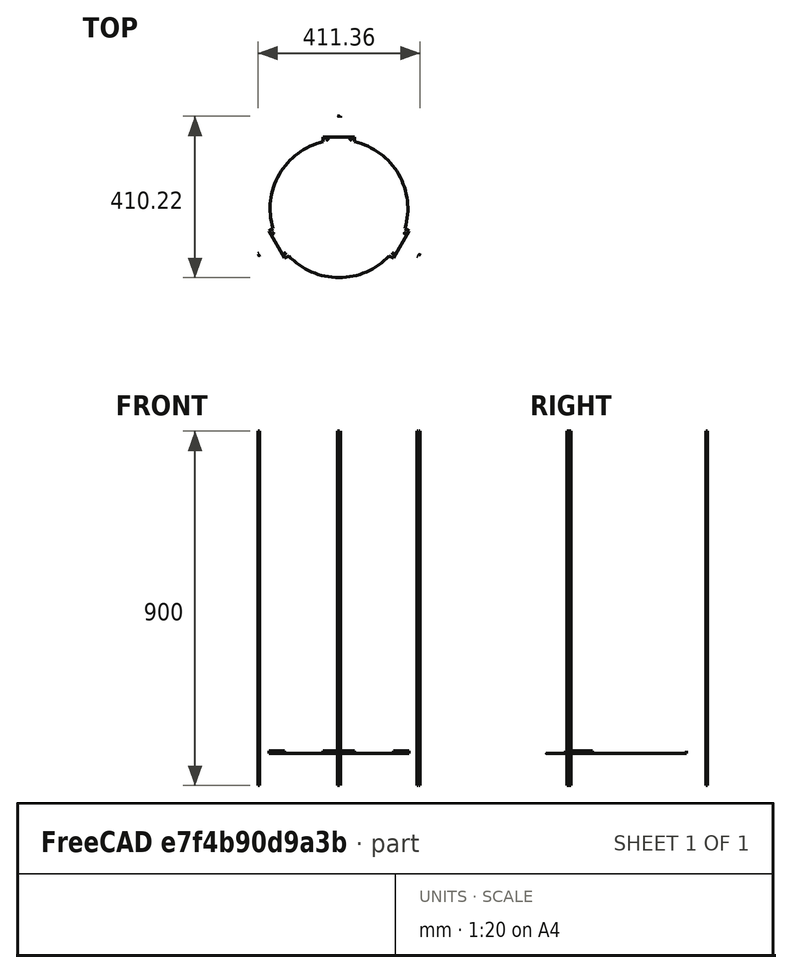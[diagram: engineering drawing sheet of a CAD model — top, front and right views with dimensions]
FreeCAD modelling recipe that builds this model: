
FCSTD DOCUMENT  (FreeCAD 2022.430R26244 +4758 (Git))
Label: SubAs3Bati
License: All rights reserved
LicenseURL: http://en.wikipedia.org/wiki/All_rights_reserved
objects: Part::FeaturePython×25, App::FeaturePython×22, App::LinkElement×3, App::Link×2
note: 24 computed .brp shape members not serialized (recipe doc carries the construction recipe); baked Part::Feature solids carry a one-line shape summary decoded from their .brp
EXTERNAL_REF file=SubAs3Column.FCStd obj=Assembly
EXTERNAL_REF file=As3bed.FCStd obj=Assembly

FEATURE [App::LinkElement] Link_i0
  LinkPlacement = pos=(263.894,-152.359,-81) rot=(0,0,1;1.0472rad)
  LinkedObject = -> <external SubAs3Column.FCStd>#Assembly
  Placement = pos=(263.894,-152.359,-81) rot=(0,0,1;1.0472rad)
  TreeRank = 0
  _LinkOwner = 4511
  _LinkVersion = 1
FEATURE [App::LinkElement] Link_i1
  LinkPlacement = pos=(-5.8111e-11,304.718,-81) rot=(0,0,1;3.14159rad)
  LinkedObject = -> <external SubAs3Column.FCStd>#Assembly
  Placement = pos=(-5.8111e-11,304.718,-81) rot=(0,0,1;3.14159rad)
  TreeRank = 0
  _LinkOwner = 4511
  _LinkVersion = 1
FEATURE [App::LinkElement] Link_i2
  LinkPlacement = pos=(-263.894,-152.359,-81) rot=(0,0,-1;1.0472rad)
  LinkedObject = -> <external SubAs3Column.FCStd>#Assembly
  Placement = pos=(-263.894,-152.359,-81) rot=(0,0,-1;1.0472rad)
  TreeRank = 0
  _LinkOwner = 4511
  _LinkVersion = 1
FEATURE [App::Link] Link  label="SubAs3Column"
  AutoLinkLabel = false
  AutoPlacement = true
  ElementCount = 3
  ElementList = -> [Link_i0,Link_i1,Link_i2]
  LinkedObject = -> <external SubAs3Column.FCStd>#Assembly
  SyncGroupVisibility = false
  TreeRank = 0
  _LinkOwner = 4510
  _LinkVersion = 1
FEATURE [App::Link] Link001  label="As3Bed"
  AutoLinkLabel = false
  AutoPlacement = true
  LinkedObject = -> <external As3bed.FCStd>#Assembly
  SyncGroupVisibility = false
  TreeRank = 0
  _LinkOwner = 4510
  _LinkVersion = 1
FEATURE [Part::FeaturePython] Parts  # WARN: FeaturePython — macro-defined, semantics opaque (R4)
  Group = -> [Link001,Link]
  GroupMode = 0
  TreeRank = 0
  _LinkVersion = 1
FEATURE [Part::FeaturePython] Assembly  label="SubAs3Bati"  # WARN: FeaturePython — macro-defined, semantics opaque (R4)
  AutoRelax = true
  BuildShape = 0
  Freeze = false
  Group = -> [Constraints,Elements,Parts]
  TreeRank = 0
  Verbose = false
  _LinkVersion = 1
  _SolverType = 1
  _Version = 1
FEATURE [App::FeaturePython] Constraints  # WARN: FeaturePython — macro-defined, semantics opaque (R4)
  Group = -> [Constraint,Constraint001,Constraint002,Constraint003,Constraint004,Constraint005,Constraint006]
  TreeRank = 0
  _LinkVersion = 1
  _Version = 1
FEATURE [App::FeaturePython] Elements  # WARN: FeaturePython — macro-defined, semantics opaque (R4)
  Group = -> [_Element,_Element001,_Element002,_Element003,_Element004,_Element005,_Element006,_Element007,_Element008,_Element009,_Element010,_Element011,Element,Element001,Element002,Element003,Element004,Element005,Element006,Element007,Element008,Element009,Element010]
  TreeRank = 0
  _LinkVersion = 1
FEATURE [App::FeaturePython] Constraint  label="Locked"  # WARN: FeaturePython — macro-defined, semantics opaque (R4)
  Disabled = false
  Group = -> [ElementLink]
  TreeRank = 0
  _ConstraintType = 0
  _LinkVersion = 1
  _Parent = -> Constraints
FEATURE [App::FeaturePython] ElementLink  label="Fix1@As3bed@"  # link proxy (typed FeaturePython)
  LinkTransform = true
  LinkedObject = -> _Element
  TreeRank = 0
  _LinkVersion = 1
  _Parent = -> Constraint
FEATURE [Part::FeaturePython] _Element  label="Fix1@As3bed@"  # link proxy (typed FeaturePython)
  Detach = false
  LinkTransform = true
  LinkedObject = -> Link001 [1.$Fix1.]
  TreeRank = 0
  _LinkVersion = 1
  _Parent = -> Elements
FEATURE [App::FeaturePython] Constraint001  label="PlaneCoincident"  # WARN: FeaturePython — macro-defined, semantics opaque (R4)
  Angle = 0
  AnglePitch = 0
  AngleRoll = 0
  Cascade = false
  Disabled = false
  Group = -> [ElementLink001,ElementLink002]
  LockAngle = false
  Multiply = false
  OffsetX = 0
  OffsetY = 0
  TreeRank = 0
  _ConstraintType = 35
  _LinkVersion = 1
  _Parent = -> Constraints
FEATURE [App::FeaturePython] ElementLink001  label="Fix1@As3bed@"  # link proxy (typed FeaturePython)
  LinkTransform = true
  LinkedObject = -> _Element
  TreeRank = 0
  _LinkVersion = 1
  _Parent = -> Constraint001
FEATURE [App::FeaturePython] ElementLink002  label="Fix3@SubAs3Column@#0"  # link proxy (typed FeaturePython)
  LinkTransform = true
  LinkedObject = -> _Element001
  TreeRank = 0
  _LinkVersion = 1
  _Parent = -> Constraint001
FEATURE [Part::FeaturePython] _Element001  label="Fix3@SubAs3Column@#0"  # link proxy (typed FeaturePython)
  Detach = false
  LinkTransform = true
  LinkedObject = -> Link [Link_i0.1.$Fix3@As3motorFrame@.]
  TreeRank = 0
  _LinkVersion = 1
  _Parent = -> Elements
FEATURE [App::FeaturePython] Constraint002  label="PlaneCoincident001"  # WARN: FeaturePython — macro-defined, semantics opaque (R4)
  Angle = 0
  AnglePitch = 0
  AngleRoll = 0
  Cascade = false
  Disabled = false
  Group = -> [ElementLink003,ElementLink004]
  LockAngle = false
  Multiply = false
  OffsetX = 0
  OffsetY = 0
  TreeRank = 0
  _ConstraintType = 35
  _LinkVersion = 1
  _Parent = -> Constraints
FEATURE [App::FeaturePython] ElementLink003  label="Fix2@As3bed@"  # link proxy (typed FeaturePython)
  LinkTransform = true
  LinkedObject = -> _Element002
  TreeRank = 0
  _LinkVersion = 1
  _Parent = -> Constraint002
FEATURE [Part::FeaturePython] _Element002  label="Fix2@As3bed@"  # link proxy (typed FeaturePython)
  Detach = false
  LinkTransform = true
  LinkedObject = -> Link001 [1.$Fix2.]
  TreeRank = 0
  _LinkVersion = 1
  _Parent = -> Elements
FEATURE [App::FeaturePython] ElementLink004  label="Fix4@SubAs3Column@#0"  # link proxy (typed FeaturePython)
  LinkTransform = true
  LinkedObject = -> _Element003
  TreeRank = 0
  _LinkVersion = 1
  _Parent = -> Constraint002
FEATURE [Part::FeaturePython] _Element003  label="Fix4@SubAs3Column@#0"  # link proxy (typed FeaturePython)
  Detach = false
  LinkTransform = true
  LinkedObject = -> Link [Link_i0.1.$Fix4@As3motorFrame@.]
  TreeRank = 0
  _LinkVersion = 1
  _Parent = -> Elements
FEATURE [App::FeaturePython] Constraint003  label="PlaneCoincident002"  # WARN: FeaturePython — macro-defined, semantics opaque (R4)
  Angle = 0
  AnglePitch = 0
  AngleRoll = 0
  Cascade = false
  Disabled = false
  Group = -> [ElementLink005,ElementLink006]
  LockAngle = false
  Multiply = false
  OffsetX = 0
  OffsetY = 0
  TreeRank = 0
  _ConstraintType = 35
  _LinkVersion = 1
  _Parent = -> Constraints
FEATURE [App::FeaturePython] ElementLink005  label="Fix3@SubAs3Column@#1"  # link proxy (typed FeaturePython)
  LinkTransform = true
  LinkedObject = -> _Element004
  TreeRank = 0
  _LinkVersion = 1
  _Parent = -> Constraint003
FEATURE [Part::FeaturePython] _Element004  label="Fix3@SubAs3Column@#1"  # link proxy (typed FeaturePython)
  Detach = false
  LinkTransform = true
  LinkedObject = -> Link [Link_i1.1.$Fix3@As3motorFrame@.]
  TreeRank = 0
  _LinkVersion = 1
  _Parent = -> Elements
FEATURE [App::FeaturePython] ElementLink006  label="Fix3@As3bed@"  # link proxy (typed FeaturePython)
  LinkTransform = true
  LinkedObject = -> _Element005
  TreeRank = 0
  _LinkVersion = 1
  _Parent = -> Constraint003
FEATURE [Part::FeaturePython] _Element005  label="Fix3@As3bed@"  # link proxy (typed FeaturePython)
  Detach = false
  LinkTransform = true
  LinkedObject = -> Link001 [1.$Fix3.]
  TreeRank = 0
  _LinkVersion = 1
  _Parent = -> Elements
FEATURE [App::FeaturePython] Constraint004  label="PlaneCoincident003"  # WARN: FeaturePython — macro-defined, semantics opaque (R4)
  Angle = 0
  AnglePitch = 0
  AngleRoll = 0
  Cascade = false
  Disabled = false
  Group = -> [ElementLink007,ElementLink008]
  LockAngle = false
  Multiply = false
  OffsetX = 0
  OffsetY = 0
  TreeRank = 0
  _ConstraintType = 35
  _LinkVersion = 1
  _Parent = -> Constraints
FEATURE [App::FeaturePython] ElementLink007  label="Fix4@SubAs3Column@#1"  # link proxy (typed FeaturePython)
  LinkTransform = true
  LinkedObject = -> _Element006
  TreeRank = 0
  _LinkVersion = 1
  _Parent = -> Constraint004
FEATURE [Part::FeaturePython] _Element006  label="Fix4@SubAs3Column@#1"  # link proxy (typed FeaturePython)
  Detach = false
  LinkTransform = true
  LinkedObject = -> Link [Link_i1.1.$Fix4@As3motorFrame@.]
  TreeRank = 0
  _LinkVersion = 1
  _Parent = -> Elements
FEATURE [App::FeaturePython] ElementLink008  label="Fix4@As3bed@"  # link proxy (typed FeaturePython)
  LinkTransform = true
  LinkedObject = -> _Element007
  TreeRank = 0
  _LinkVersion = 1
  _Parent = -> Constraint004
FEATURE [Part::FeaturePython] _Element007  label="Fix4@As3bed@"  # link proxy (typed FeaturePython)
  Detach = false
  LinkTransform = true
  LinkedObject = -> Link001 [1.$Fix4.]
  TreeRank = 0
  _LinkVersion = 1
  _Parent = -> Elements
FEATURE [App::FeaturePython] Constraint005  label="PlaneCoincident004"  # WARN: FeaturePython — macro-defined, semantics opaque (R4)
  Angle = 0
  AnglePitch = 0
  AngleRoll = 0
  Cascade = false
  Disabled = false
  Group = -> [ElementLink009,ElementLink010]
  LockAngle = false
  Multiply = false
  OffsetX = 0
  OffsetY = 0
  TreeRank = 0
  _ConstraintType = 35
  _LinkVersion = 1
  _Parent = -> Constraints
FEATURE [App::FeaturePython] ElementLink009  label="Fix3@SubAs3Column@#2"  # link proxy (typed FeaturePython)
  LinkTransform = true
  LinkedObject = -> _Element008
  TreeRank = 0
  _LinkVersion = 1
  _Parent = -> Constraint005
FEATURE [Part::FeaturePython] _Element008  label="Fix3@SubAs3Column@#2"  # link proxy (typed FeaturePython)
  Detach = false
  LinkTransform = true
  LinkedObject = -> Link [Link_i2.1.$Fix3@As3motorFrame@.]
  TreeRank = 0
  _LinkVersion = 1
  _Parent = -> Elements
FEATURE [App::FeaturePython] ElementLink010  label="Fix5@As3bed@"  # link proxy (typed FeaturePython)
  LinkTransform = true
  LinkedObject = -> _Element009
  TreeRank = 0
  _LinkVersion = 1
  _Parent = -> Constraint005
FEATURE [Part::FeaturePython] _Element009  label="Fix5@As3bed@"  # link proxy (typed FeaturePython)
  Detach = false
  LinkTransform = true
  LinkedObject = -> Link001 [1.$Fix5.]
  TreeRank = 0
  _LinkVersion = 1
  _Parent = -> Elements
FEATURE [App::FeaturePython] Constraint006  label="PlaneCoincident005"  # WARN: FeaturePython — macro-defined, semantics opaque (R4)
  Angle = 0
  AnglePitch = 0
  AngleRoll = 0
  Cascade = false
  Disabled = false
  Group = -> [ElementLink011,ElementLink012]
  LockAngle = false
  Multiply = false
  OffsetX = 0
  OffsetY = 0
  TreeRank = 0
  _ConstraintType = 35
  _LinkVersion = 1
  _Parent = -> Constraints
FEATURE [App::FeaturePython] ElementLink011  label="Fix4@SubAs3Column@#2"  # link proxy (typed FeaturePython)
  LinkTransform = true
  LinkedObject = -> _Element010
  TreeRank = 0
  _LinkVersion = 1
  _Parent = -> Constraint006
FEATURE [Part::FeaturePython] _Element010  label="Fix4@SubAs3Column@#2"  # link proxy (typed FeaturePython)
  Detach = false
  LinkTransform = true
  LinkedObject = -> Link [Link_i2.1.$Fix4@As3motorFrame@.]
  TreeRank = 0
  _LinkVersion = 1
  _Parent = -> Elements
FEATURE [App::FeaturePython] ElementLink012  label="Fix6@As3bed@"  # link proxy (typed FeaturePython)
  LinkTransform = true
  LinkedObject = -> _Element011
  TreeRank = 0
  _LinkVersion = 1
  _Parent = -> Constraint006
FEATURE [Part::FeaturePython] _Element011  label="Fix6@As3bed@"  # link proxy (typed FeaturePython)
  Detach = false
  LinkTransform = true
  LinkedObject = -> Link001 [1.$Fix6.]
  TreeRank = 0
  _LinkVersion = 1
  _Parent = -> Elements
FEATURE [Part::FeaturePython] Element  label="Fix@SubAs3Column@#0"  # link proxy (typed FeaturePython)
  Detach = false
  LinkTransform = true
  LinkedObject = -> Link [Link_i0.1.$Fix@As3MGNR9R900CM-HiwinCorporation-3D-10-31-2021@.]
  TreeRank = 0
  _LinkVersion = 1
  _Parent = -> Elements
FEATURE [Part::FeaturePython] Element001  label="Ref@SubAs3Column@#0"  # link proxy (typed FeaturePython)
  Detach = false
  LinkTransform = true
  LinkedObject = -> Link [Link_i0.1.$Ref@As3MGNR9R900CM-HiwinCorporation-3D-10-31-2021@.]
  TreeRank = 0
  _LinkVersion = 1
  _Parent = -> Elements
FEATURE [Part::FeaturePython] Element002  label="Lat@SubAs3Column@#0"  # link proxy (typed FeaturePython)
  Detach = false
  LinkTransform = true
  LinkedObject = -> Link [Link_i0.1.$Lat@As3MGNR9R900CM-HiwinCorporation-3D-10-31-2021@.]
  TreeRank = 0
  _LinkVersion = 1
  _Parent = -> Elements
FEATURE [Part::FeaturePython] Element003  label="Ref@SubAs3Column@#1"  # link proxy (typed FeaturePython)
  Detach = false
  LinkTransform = true
  LinkedObject = -> Link [Link_i1.1.$Ref@As3MGNR9R900CM-HiwinCorporation-3D-10-31-2021@.]
  TreeRank = 0
  _LinkVersion = 1
  _Parent = -> Elements
FEATURE [Part::FeaturePython] Element004  label="Lat@SubAs3Column@#1"  # link proxy (typed FeaturePython)
  Detach = false
  LinkTransform = true
  LinkedObject = -> Link [Link_i1.1.$Lat@As3MGNR9R900CM-HiwinCorporation-3D-10-31-2021@.]
  TreeRank = 0
  _LinkVersion = 1
  _Parent = -> Elements
FEATURE [Part::FeaturePython] Element005  label="Ref@SubAs3Column@#2"  # link proxy (typed FeaturePython)
  Detach = false
  LinkTransform = true
  LinkedObject = -> Link [Link_i2.1.$Ref@As3MGNR9R900CM-HiwinCorporation-3D-10-31-2021@.]
  TreeRank = 0
  _LinkVersion = 1
  _Parent = -> Elements
FEATURE [Part::FeaturePython] Element006  label="Lat@SubAs3Column@#2"  # link proxy (typed FeaturePython)
  Detach = false
  LinkTransform = true
  LinkedObject = -> Link [Link_i2.1.$Lat@As3MGNR9R900CM-HiwinCorporation-3D-10-31-2021@.]
  TreeRank = 0
  _LinkVersion = 1
  _Parent = -> Elements
FEATURE [Part::FeaturePython] Element007  # link proxy (typed FeaturePython)
  Detach = false
  LinkTransform = true
  LinkedObject = -> Link001 [1.$Element006.]
  TreeRank = 0
  _LinkVersion = 1
  _Parent = -> Elements
FEATURE [Part::FeaturePython] Element008  # link proxy (typed FeaturePython)
  Detach = false
  LinkTransform = true
  LinkedObject = -> Link001 [1.$Element007.]
  TreeRank = 0
  _LinkVersion = 1
  _Parent = -> Elements
FEATURE [Part::FeaturePython] Element009  # link proxy (typed FeaturePython)
  Detach = false
  LinkTransform = true
  LinkedObject = -> Link001 [1.$Element008.]
  TreeRank = 0
  _LinkVersion = 1
  _Parent = -> Elements
FEATURE [Part::FeaturePython] Element010  # link proxy (typed FeaturePython)
  Detach = false
  LinkTransform = true
  LinkedObject = -> Link001 [1.$Element009.]
  TreeRank = 0
  _LinkVersion = 1
  _Parent = -> Elements

RESOLVED EXTERNAL PARTS (link-assembly join: the EXTERNAL_REF files above that resolve inside this repo's crawl, each included once):
---- part As3bed.FCStd = doc fcstd_8b39a00332d4 ----
FCSTD DOCUMENT  (FreeCAD 2022.430R26244 +4758 (Git))
Label: As3bed
License: All rights reserved
LicenseURL: http://en.wikipedia.org/wiki/All_rights_reserved
objects: Part::FeaturePython×12, App::FeaturePython×2, App::Link×1
note: 11 computed .brp shape members not serialized (recipe doc carries the construction recipe); baked Part::Feature solids carry a one-line shape summary decoded from their .brp
EXTERNAL_REF file=Bed.FCStd obj=Bed

FEATURE [App::FeaturePython] Constraints  # WARN: FeaturePython — macro-defined, semantics opaque (R4)
  TreeRank = 0
  _LinkVersion = 1
  _Version = 1
FEATURE [App::Link] Link  label="Bed"
  AutoLinkLabel = false
  AutoPlacement = true
  LinkedObject = -> <external Bed.FCStd>#Bed
  SyncGroupVisibility = false
  TreeRank = 0
  _LinkOwner = 131
  _LinkVersion = 1
FEATURE [Part::FeaturePython] Parts  # WARN: FeaturePython — macro-defined, semantics opaque (R4)
  Group = -> [Link]
  GroupMode = 0
  TreeRank = 0
  _LinkVersion = 1
FEATURE [Part::FeaturePython] Assembly  label="As3Bed"  # WARN: FeaturePython — macro-defined, semantics opaque (R4)
  AutoRelax = true
  BuildShape = 0
  Freeze = false
  Group = -> [Constraints,Elements,Parts]
  TreeRank = 0
  Verbose = false
  _LinkVersion = 1
  _SolverType = 1
  _Version = 1
FEATURE [App::FeaturePython] Elements  # WARN: FeaturePython — macro-defined, semantics opaque (R4)
  Group = -> [Element,Element001,Element002,Element004,Element003,Element005,Element006,Element007,Element008,Element009]
  TreeRank = 0
  _LinkVersion = 1
FEATURE [Part::FeaturePython] Element  label="Fix1"  # link proxy (typed FeaturePython)
  Detach = false
  LinkTransform = true
  LinkedObject = -> Link [PolarPattern.Edge23]
  TreeRank = 0
  _LinkVersion = 1
  _Parent = -> Elements
FEATURE [Part::FeaturePython] Element001  label="Fix2"  # link proxy (typed FeaturePython)
  Detach = false
  LinkTransform = true
  LinkedObject = -> Link [PolarPattern.Edge20]
  TreeRank = 0
  _LinkVersion = 1
  _Parent = -> Elements
FEATURE [Part::FeaturePython] Element002  label="Fix3"  # link proxy (typed FeaturePython)
  Detach = false
  LinkTransform = true
  LinkedObject = -> Link [PolarPattern.Edge21]
  TreeRank = 0
  _LinkVersion = 1
  _Parent = -> Elements
FEATURE [Part::FeaturePython] Element003  label="Fix5"  # link proxy (typed FeaturePython)
  Detach = false
  LinkTransform = true
  LinkedObject = -> Link [PolarPattern.Edge24]
  TreeRank = 0
  _LinkVersion = 1
  _Parent = -> Elements
FEATURE [Part::FeaturePython] Element004  label="Fix4"  # link proxy (typed FeaturePython)
  Detach = false
  LinkTransform = true
  LinkedObject = -> Link [PolarPattern.Edge25]
  TreeRank = 0
  _LinkVersion = 1
  _Parent = -> Elements
FEATURE [Part::FeaturePython] Element005  label="Fix6"  # link proxy (typed FeaturePython)
  Detach = false
  LinkTransform = true
  LinkedObject = -> Link [PolarPattern.Edge22]
  TreeRank = 0
  _LinkVersion = 1
  _Parent = -> Elements
FEATURE [Part::FeaturePython] Element006  # link proxy (typed FeaturePython)
  Detach = false
  LinkTransform = true
  LinkedObject = -> Link [PolarPattern.Face4]
  TreeRank = 0
  _LinkVersion = 1
  _Parent = -> Elements
FEATURE [Part::FeaturePython] Element007  # link proxy (typed FeaturePython)
  Detach = false
  LinkTransform = true
  LinkedObject = -> Link [PolarPattern.Face26]
  TreeRank = 0
  _LinkVersion = 1
  _Parent = -> Elements
FEATURE [Part::FeaturePython] Element008  # link proxy (typed FeaturePython)
  Detach = false
  LinkTransform = true
  LinkedObject = -> Link [PolarPattern.Face25]
  TreeRank = 0
  _LinkVersion = 1
  _Parent = -> Elements
FEATURE [Part::FeaturePython] Element009  # link proxy (typed FeaturePython)
  Detach = false
  LinkTransform = true
  LinkedObject = -> Link [PolarPattern.Face24]
  TreeRank = 0
  _LinkVersion = 1
  _Parent = -> Elements
---- part SubAs3Column.FCStd = doc fcstd_332bf76e1e08 ----
FCSTD DOCUMENT  (FreeCAD 2022.430R26244 +4758 (Git))
Label: SubAs3Column
License: All rights reserved
LicenseURL: http://en.wikipedia.org/wiki/All_rights_reserved
objects: App::FeaturePython×82, Part::FeaturePython×48, App::Link×8, App::LinkElement×3
note: 47 computed .brp shape members not serialized (recipe doc carries the construction recipe); baked Part::Feature solids carry a one-line shape summary decoded from their .brp
EXTERNAL_REF file=as3bottom_corner-M3x10.FCStd obj=Assembly
EXTERNAL_REF file=as3V-Slot 20x40x1000 Linear Rail.FCStd obj=Assembly
EXTERNAL_REF file=as3V-Slot 20x60x1000 Linear Rail.FCStd obj=Assembly
EXTERNAL_REF file=as3OpenBeam450mm.FCStd obj=Assembly
EXTERNAL_REF file=as3MotorFrame.FCStd obj=Assembly
EXTERNAL_REF file=As3NEMA 17.FCStd obj=Assembly
EXTERNAL_REF file=As3TopCorner.FCStd obj=Assembly
EXTERNAL_REF file=as3MGNR9R900CM-HiwinCorporation-3D-10-31-2021.FCStd obj=Assembly

FEATURE [App::Link] Link  label="As3bottom_corner-M3x10"
  AutoLinkLabel = false
  AutoPlacement = true
  LinkedObject = -> <external as3bottom_corner-M3x10.FCStd>#Assembly
  SyncGroupVisibility = false
  TreeRank = 0
  _LinkOwner = 170
  _LinkVersion = 1
FEATURE [App::Link] Link001  label="As3V-Slot 20x40x1000 Linear Rail"
  AutoLinkLabel = false
  AutoPlacement = true
  LinkPlacement = pos=(3.1367e-12,50,0) rot=(0,0,1;0rad)
  LinkedObject = -> <external as3V-Slot 20x40x1000 Linear Rail.FCStd>#Assembly
  Placement = pos=(3.1367e-12,50,0) rot=(0,0,1;0rad)
  SyncGroupVisibility = false
  TreeRank = 0
  _LinkOwner = 170
  _LinkVersion = 1
FEATURE [App::Link] Link002  label="As3V-Slot 20x60x1000 Linear Rail"
  AutoLinkLabel = false
  AutoPlacement = true
  LinkPlacement = pos=(0.1,20,1.28e-14) rot=(0,0,1;1.5708rad)
  LinkedObject = -> <external as3V-Slot 20x60x1000 Linear Rail.FCStd>#Assembly
  Placement = pos=(0.1,20,1.28e-14) rot=(0,0,1;1.5708rad)
  SyncGroupVisibility = false
  TreeRank = 0
  _LinkOwner = 170
  _LinkVersion = 1
FEATURE [App::LinkElement] Link003_i0
  LinkPlacement = pos=(310.961,131.486,64) rot=(0.866025,0.5,0;3.14159rad)
  LinkedObject = -> <external as3OpenBeam450mm.FCStd>#Assembly
  Placement = pos=(310.961,131.486,64) rot=(0.866025,0.5,0;3.14159rad)
  TreeRank = 0
  _LinkOwner = 191
  _LinkVersion = 1
FEATURE [App::LinkElement] Link003_i1
  LinkPlacement = pos=(1.39218,310.216,16) rot=(0,0,1;1.0472rad)
  LinkedObject = -> <external as3OpenBeam450mm.FCStd>#Assembly
  Placement = pos=(1.39218,310.216,16) rot=(0,0,1;1.0472rad)
  TreeRank = 0
  _LinkOwner = 191
  _LinkVersion = 1
FEATURE [App::LinkElement] Link003_i2
  LinkPlacement = pos=(0.13852,308.365,986) rot=(0,0,1;1.0472rad)
  LinkedObject = -> <external as3OpenBeam450mm.FCStd>#Assembly
  Placement = pos=(0.13852,308.365,986) rot=(0,0,1;1.0472rad)
  TreeRank = 0
  _LinkOwner = 191
  _LinkVersion = 1
FEATURE [App::Link] Link003  label="As3OpenBeam450mm"
  AutoLinkLabel = false
  AutoPlacement = true
  ElementCount = 3
  ElementList = -> [Link003_i0,Link003_i1,Link003_i2]
  LinkedObject = -> <external as3OpenBeam450mm.FCStd>#Assembly
  SyncGroupVisibility = false
  TreeRank = 0
  _LinkOwner = 170
  _LinkVersion = 1
FEATURE [App::Link] Link004  label="As3motorFrame"
  AutoLinkLabel = false
  AutoPlacement = true
  LinkPlacement = pos=(1.81557e-11,50.2887,11) rot=(0,0,1;0rad)
  LinkedObject = -> <external as3MotorFrame.FCStd>#Assembly
  Placement = pos=(1.81557e-11,50.2887,11) rot=(0,0,1;0rad)
  SyncGroupVisibility = false
  TreeRank = 0
  _LinkOwner = 170
  _LinkVersion = 1
FEATURE [App::Link] Link005  label="As3NEMA 17"
  AutoLinkLabel = false
  AutoPlacement = true
  LinkPlacement = pos=(-10.3955,158.351,45.6172) rot=(0,-0.707107,0.707107;3.14159rad)
  LinkedObject = -> <external As3NEMA 17.FCStd>#Assembly
  Placement = pos=(-10.3955,158.351,45.6172) rot=(0,-0.707107,0.707107;3.14159rad)
  SyncGroupVisibility = false
  TreeRank = 0
  _LinkOwner = 170
  _LinkVersion = 1
FEATURE [App::Link] Link006  label="As3top_corner"
  AutoLinkLabel = false
  AutoPlacement = true
  LinkPlacement = pos=(4.59e-14,11,1000) rot=(0,-1,0;3.14159rad)
  LinkedObject = -> <external As3TopCorner.FCStd>#Assembly
  Placement = pos=(4.59e-14,11,1000) rot=(0,-1,0;3.14159rad)
  SyncGroupVisibility = false
  TreeRank = 0
  _LinkOwner = 170
  _LinkVersion = 1
FEATURE [App::Link] Link007  label="As3MGNR9R900CM-HiwinCorporation-3D-10-31-2021"
  AutoLinkLabel = false
  AutoPlacement = true
  LinkPlacement = pos=(3.296e-12,69.5,892.5) rot=(0.57735,-0.57735,-0.57735;4.18879rad)
  LinkedObject = -> <external as3MGNR9R900CM-HiwinCorporation-3D-10-31-2021.FCStd>#Assembly
  Placement = pos=(3.296e-12,69.5,892.5) rot=(0.57735,-0.57735,-0.57735;4.18879rad)
  SyncGroupVisibility = false
  TreeRank = 0
  _LinkOwner = 170
  _LinkVersion = 1
FEATURE [Part::FeaturePython] Parts  # WARN: FeaturePython — macro-defined, semantics opaque (R4)
  Group = -> [Link,Link002,Link003,Link004,Link005,Link006,Link001,Link007]
  GroupMode = 0
  TreeRank = 0
  _LinkVersion = 1
FEATURE [Part::FeaturePython] Assembly  label="SubAs3Column"  # WARN: FeaturePython — macro-defined, semantics opaque (R4)
  AutoRelax = true
  BuildShape = 0
  Freeze = false
  Group = -> [Constraints,Elements,Parts]
  TreeRank = 0
  Verbose = false
  _LinkVersion = 1
  _SolverType = 1
  _Version = 1
FEATURE [App::FeaturePython] Constraints  # WARN: FeaturePython — macro-defined, semantics opaque (R4)
  Group = -> [Constraint,Constraint001,Constraint002,Constraint003,Constraint004,Constraint005,Constraint006,Constraint007,Constraint008,Constraint009,Constraint010,Constraint011,Constraint012,Constraint013,Constraint014,Constraint016,Constraint017,Constraint015,Constraint019,Constraint020,Constraint018,Constraint021,Constraint022,Constraint023,Constraint024,Constraint025,Constraint026]
  TreeRank = 0
  _LinkVersion = 1
  _Version = 1
FEATURE [App::FeaturePython] Elements  # WARN: FeaturePython — macro-defined, semantics opaque (R4)
  Group = -> [_Element,_Element001,_Element002,_Element003,_Element004,_Element005,_Element006,_Element007,_Element008,_Element009,_Element010,_Element011,_Element012,_Element013,_Element014,_Element015,_Element016,_Element017,_Element018,_Element019,_Element020,_Element021,_Element022,_Element023,_Element024,_Element025,_Element026,_Element027,_Element028,_Element029,_Element030,_Element031,_Element032,+13 more]
  TreeRank = 0
  _LinkVersion = 1
FEATURE [App::FeaturePython] Constraint  label="Locked"  # WARN: FeaturePython — macro-defined, semantics opaque (R4)
  Disabled = false
  Group = -> [ElementLink]
  TreeRank = 0
  _ConstraintType = 0
  _LinkVersion = 1
  _Parent = -> Constraints
FEATURE [App::FeaturePython] ElementLink  label="_Element"  # link proxy (typed FeaturePython)
  LinkTransform = true
  LinkedObject = -> _Element
  TreeRank = 0
  _LinkVersion = 1
  _Parent = -> Constraint
FEATURE [Part::FeaturePython] _Element  # link proxy (typed FeaturePython)
  Detach = false
  LinkTransform = true
  LinkedObject = -> Link [1.$FaceRef.]
  TreeRank = 0
  _LinkVersion = 1
  _Parent = -> Elements
FEATURE [App::FeaturePython] Constraint001  label="PlaneAlignment"  # WARN: FeaturePython — macro-defined, semantics opaque (R4)
  Angle = 0
  AnglePitch = 0
  AngleRoll = 0
  Cascade = false
  Disabled = false
  Group = -> [ElementLink001,ElementLink002]
  LockAngle = false
  TreeRank = 0
  _ConstraintType = 37
  _LinkVersion = 1
  _Parent = -> Constraints
FEATURE [App::FeaturePython] ElementLink001  label="_Element001"  # link proxy (typed FeaturePython)
  LinkTransform = true
  LinkedObject = -> _Element001
  TreeRank = 0
  _LinkVersion = 1
  _Parent = -> Constraint001
FEATURE [Part::FeaturePython] _Element001  # link proxy (typed FeaturePython)
  Detach = false
  LinkTransform = true
  LinkedObject = -> Link002 [1.$FaceVref.]
  TreeRank = 0
  _LinkVersion = 1
  _Parent = -> Elements
FEATURE [App::FeaturePython] ElementLink002  label="_Element002"  # link proxy (typed FeaturePython)
  LinkTransform = true
  LinkedObject = -> _Element002
  TreeRank = 0
  _LinkVersion = 1
  _Parent = -> Constraint001
FEATURE [Part::FeaturePython] _Element002  # link proxy (typed FeaturePython)
  Detach = false
  LinkTransform = true
  LinkedObject = -> Link [1.$AppuiPoteau1.]
  TreeRank = 0
  _LinkVersion = 1
  _Parent = -> Elements
FEATURE [App::FeaturePython] Constraint002  label="PlaneAlignment001"  # WARN: FeaturePython — macro-defined, semantics opaque (R4)
  Angle = 0
  AnglePitch = 0
  AngleRoll = 0
  Cascade = false
  Disabled = false
  Group = -> [ElementLink003,ElementLink004]
  LockAngle = false
  TreeRank = 0
  _ConstraintType = 37
  _LinkVersion = 1
  _Parent = -> Constraints
FEATURE [App::FeaturePython] ElementLink003  label="_Element003"  # link proxy (typed FeaturePython)
  LinkTransform = true
  LinkedObject = -> _Element003
  TreeRank = 0
  _LinkVersion = 1
  _Parent = -> Constraint002
FEATURE [Part::FeaturePython] _Element003  # link proxy (typed FeaturePython)
  Detach = false
  LinkTransform = true
  LinkedObject = -> Link002 [1.$FaceLat.]
  TreeRank = 0
  _LinkVersion = 1
  _Parent = -> Elements
FEATURE [App::FeaturePython] ElementLink004  label="_Element004"  # link proxy (typed FeaturePython)
  LinkTransform = true
  LinkedObject = -> _Element004
  TreeRank = 0
  _LinkVersion = 1
  _Parent = -> Constraint002
FEATURE [Part::FeaturePython] _Element004  # link proxy (typed FeaturePython)
  Detach = false
  LinkTransform = true
  LinkedObject = -> Link [1.$AppuiPoteau2.]
  TreeRank = 0
  _LinkVersion = 1
  _Parent = -> Elements
FEATURE [App::FeaturePython] Constraint003  label="PlaneAlignment002"  # WARN: FeaturePython — macro-defined, semantics opaque (R4)
  Angle = 0
  AnglePitch = 0
  AngleRoll = 0
  Cascade = false
  Disabled = false
  Group = -> [ElementLink005,ElementLink006]
  LockAngle = false
  TreeRank = 0
  _ConstraintType = 37
  _LinkVersion = 1
  _Parent = -> Constraints
FEATURE [App::FeaturePython] ElementLink005  label="_Element005"  # link proxy (typed FeaturePython)
  LinkTransform = true
  LinkedObject = -> _Element005
  TreeRank = 0
  _LinkVersion = 1
  _Parent = -> Constraint003
FEATURE [Part::FeaturePython] _Element005  # link proxy (typed FeaturePython)
  Detach = false
  LinkTransform = true
  LinkedObject = -> Link002 [1.$Extrem1.]
  TreeRank = 0
  _LinkVersion = 1
  _Parent = -> Elements
FEATURE [App::FeaturePython] ElementLink006  label="_Element"  # link proxy (typed FeaturePython)
  LinkTransform = true
  LinkedObject = -> _Element
  TreeRank = 0
  _LinkVersion = 1
  _Parent = -> Constraint003
FEATURE [App::FeaturePython] Constraint004  label="PlaneAlignment003"  # WARN: FeaturePython — macro-defined, semantics opaque (R4)
  Angle = 0
  AnglePitch = 0
  AngleRoll = 0
  Cascade = false
  Disabled = false
  Group = -> [ElementLink007,ElementLink008]
  LockAngle = false
  TreeRank = 0
  _ConstraintType = 37
  _LinkVersion = 1
  _Parent = -> Constraints
FEATURE [App::FeaturePython] ElementLink007  label="AppuiTrv1v@As3bottom_corner-M3x10@"  # link proxy (typed FeaturePython)
  LinkTransform = true
  LinkedObject = -> _Element006
  TreeRank = 0
  _LinkVersion = 1
  _Parent = -> Constraint004
FEATURE [Part::FeaturePython] _Element006  label="AppuiTrv1v@As3bottom_corner-M3x10@"  # link proxy (typed FeaturePython)
  Detach = false
  LinkTransform = true
  LinkedObject = -> Link [1.$AppuiTrav1v.]
  TreeRank = 0
  _LinkVersion = 1
  _Parent = -> Elements
FEATURE [App::FeaturePython] ElementLink008  label="FaceLat2@As3OpenBeam450mm@#0"  # link proxy (typed FeaturePython)
  LinkTransform = true
  LinkedObject = -> _Element016
  Placement = pos=(-5.68e-14,0,0) rot=(0,0,1;0rad)
  TreeRank = 0
  _LinkVersion = 1
  _Parent = -> Constraint004
FEATURE [Part::FeaturePython] _Element007  label="FaceLat@As3OpenBeam450mm@#0"  # link proxy (typed FeaturePython)
  Detach = false
  LinkTransform = true
  LinkedObject = -> Link003 [Link003_i0.1.$FaceLat1.]
  TreeRank = 0
  _LinkVersion = 1
  _Parent = -> Elements
FEATURE [App::FeaturePython] Constraint005  label="PlaneAlignment004"  # WARN: FeaturePython — macro-defined, semantics opaque (R4)
  Angle = 0
  AnglePitch = 0
  AngleRoll = 0
  Cascade = false
  Disabled = false
  Group = -> [ElementLink009,ElementLink010]
  LockAngle = false
  TreeRank = 0
  _ConstraintType = 37
  _LinkVersion = 1
  _Parent = -> Constraints
FEATURE [App::FeaturePython] ElementLink009  label="FaceHoriz@As3OpenBeam450mm@#0"  # link proxy (typed FeaturePython)
  LinkTransform = true
  LinkedObject = -> _Element008
  Placement = pos=(2.84e-14,-2.84e-14,0) rot=(0,0,1;0rad)
  TreeRank = 0
  _LinkVersion = 1
  _Parent = -> Constraint005
FEATURE [Part::FeaturePython] _Element008  label="FaceHoriz@As3OpenBeam450mm@#0"  # link proxy (typed FeaturePython)
  Detach = false
  LinkTransform = true
  LinkedObject = -> Link003 [Link003_i0.1.$FaceHoriz1.]
  TreeRank = 0
  _LinkVersion = 1
  _Parent = -> Elements
FEATURE [App::FeaturePython] ElementLink010  label="AppuiTrav1h@As3bottom_corner-M3x10@"  # link proxy (typed FeaturePython)
  LinkTransform = true
  LinkedObject = -> _Element009
  TreeRank = 0
  _LinkVersion = 1
  _Parent = -> Constraint005
FEATURE [Part::FeaturePython] _Element009  label="AppuiTrav1h@As3bottom_corner-M3x10@"  # link proxy (typed FeaturePython)
  Detach = false
  LinkTransform = true
  LinkedObject = -> Link [1.$AppuiTrav1h.]
  TreeRank = 0
  _LinkVersion = 1
  _Parent = -> Elements
FEATURE [App::FeaturePython] Constraint006  label="PlaneAlignment005"  # WARN: FeaturePython — macro-defined, semantics opaque (R4)
  Angle = 0
  AnglePitch = 0
  AngleRoll = 0
  Cascade = false
  Disabled = false
  Group = -> [ElementLink011,ElementLink012]
  LockAngle = false
  TreeRank = 0
  _ConstraintType = 37
  _LinkVersion = 1
  _Parent = -> Constraints
FEATURE [App::FeaturePython] ElementLink011  label="FaceHoriz@As3OpenBeam450mm@#1"  # link proxy (typed FeaturePython)
  LinkTransform = true
  LinkedObject = -> _Element010
  TreeRank = 0
  _LinkVersion = 1
  _Parent = -> Constraint006
FEATURE [Part::FeaturePython] _Element010  label="FaceHoriz@As3OpenBeam450mm@#1"  # link proxy (typed FeaturePython)
  Detach = false
  LinkTransform = true
  LinkedObject = -> Link003 [Link003_i1.1.$FaceHoriz1.]
  TreeRank = 0
  _LinkVersion = 1
  _Parent = -> Elements
FEATURE [App::FeaturePython] ElementLink012  label="AppuiTrav2h@As3bottom_corner-M3x10@"  # link proxy (typed FeaturePython)
  LinkTransform = true
  LinkedObject = -> _Element011
  TreeRank = 0
  _LinkVersion = 1
  _Parent = -> Constraint006
FEATURE [Part::FeaturePython] _Element011  label="AppuiTrav2h@As3bottom_corner-M3x10@"  # link proxy (typed FeaturePython)
  Detach = false
  LinkTransform = true
  LinkedObject = -> Link [1.$AppuiTrav2h.]
  TreeRank = 0
  _LinkVersion = 1
  _Parent = -> Elements
FEATURE [App::FeaturePython] Constraint007  label="PlaneAlignment006"  # WARN: FeaturePython — macro-defined, semantics opaque (R4)
  Angle = 0
  AnglePitch = 0
  AngleRoll = 0
  Cascade = false
  Disabled = false
  Group = -> [ElementLink013,ElementLink014]
  LockAngle = false
  TreeRank = 0
  _ConstraintType = 37
  _LinkVersion = 1
  _Parent = -> Constraints
FEATURE [App::FeaturePython] ElementLink013  label="AppuiTrv1v@As3bottom_corner-M3x10@"  # link proxy (typed FeaturePython)
  LinkTransform = true
  LinkedObject = -> _Element006
  Placement = pos=(0,1.42e-14,2.84e-14) rot=(0,0,1;0rad)
  TreeRank = 0
  _LinkVersion = 1
  _Parent = -> Constraint007
FEATURE [App::FeaturePython] ElementLink014  label="FaceLat@As3OpenBeam450mm@#1"  # link proxy (typed FeaturePython)
  LinkTransform = true
  LinkedObject = -> _Element012
  Placement = pos=(5.68e-14,-2.84e-14,-1.8e-15) rot=(0,0,1;0rad)
  TreeRank = 0
  _LinkVersion = 1
  _Parent = -> Constraint007
FEATURE [Part::FeaturePython] _Element012  label="FaceLat@As3OpenBeam450mm@#1"  # link proxy (typed FeaturePython)
  Detach = false
  LinkTransform = true
  LinkedObject = -> Link003 [Link003_i1.1.$FaceLat1.]
  TreeRank = 0
  _LinkVersion = 1
  _Parent = -> Elements
FEATURE [Part::FeaturePython] _Element013  label="Extrem1@As3OpenBeam450mm@#0"  # link proxy (typed FeaturePython)
  Detach = false
  LinkTransform = true
  LinkedObject = -> Link003 [Link003_i0.1.$Extrem1.]
  TreeRank = 0
  _LinkVersion = 1
  _Parent = -> Elements
FEATURE [Part::FeaturePython] _Element014  label="Extrem1@As3OpenBeam450mm@#1"  # link proxy (typed FeaturePython)
  Detach = false
  LinkTransform = true
  LinkedObject = -> Link003 [Link003_i1.1.$Extrem1.]
  TreeRank = 0
  _LinkVersion = 1
  _Parent = -> Elements
FEATURE [Part::FeaturePython] _Element015  label="ExtremRain1@As3bottom_corner-M3x10@"  # link proxy (typed FeaturePython)
  Detach = false
  LinkTransform = true
  LinkedObject = -> Link [1.$ExtremRain1.]
  TreeRank = 0
  _LinkVersion = 1
  _Parent = -> Elements
FEATURE [App::FeaturePython] Constraint008  label="PlaneAlignment007"  # WARN: FeaturePython — macro-defined, semantics opaque (R4)
  Angle = 0
  AnglePitch = 0
  AngleRoll = 0
  Cascade = false
  Disabled = false
  Group = -> [ElementLink015,ElementLink016]
  LockAngle = false
  TreeRank = 0
  _ConstraintType = 37
  _LinkVersion = 1
  _Parent = -> Constraints
FEATURE [App::FeaturePython] ElementLink015  label="ExtremRain1@As3bottom_corner-M3x10@"  # link proxy (typed FeaturePython)
  LinkTransform = true
  LinkedObject = -> _Element015
  TreeRank = 0
  _LinkVersion = 1
  _Parent = -> Constraint008
FEATURE [App::FeaturePython] ElementLink016  label="Extrem1@As3OpenBeam450mm@#0"  # link proxy (typed FeaturePython)
  LinkTransform = true
  LinkedObject = -> _Element013
  TreeRank = 0
  _LinkVersion = 1
  _Parent = -> Constraint008
FEATURE [App::FeaturePython] Constraint009  label="PlaneAlignment008"  # WARN: FeaturePython — macro-defined, semantics opaque (R4)
  Angle = 0
  AnglePitch = 0
  AngleRoll = 0
  Cascade = false
  Disabled = false
  Group = -> [ElementLink017,ElementLink018]
  LockAngle = false
  TreeRank = 0
  _ConstraintType = 37
  _LinkVersion = 1
  _Parent = -> Constraints
FEATURE [App::FeaturePython] ElementLink017  label="ExtremRain1@As3bottom_corner-M3x10@"  # link proxy (typed FeaturePython)
  LinkTransform = true
  LinkedObject = -> _Element015
  TreeRank = 0
  _LinkVersion = 1
  _Parent = -> Constraint009
FEATURE [App::FeaturePython] ElementLink018  label="Extrem1@As3OpenBeam450mm@#1"  # link proxy (typed FeaturePython)
  LinkTransform = true
  LinkedObject = -> _Element014
  TreeRank = 0
  _LinkVersion = 1
  _Parent = -> Constraint009
FEATURE [Part::FeaturePython] _Element016  label="FaceLat2@As3OpenBeam450mm@#0"  # link proxy (typed FeaturePython)
  Detach = false
  LinkTransform = true
  LinkedObject = -> Link003 [Link003_i0.1.$FaceLat2.]
  TreeRank = 0
  _LinkVersion = 1
  _Parent = -> Elements
FEATURE [App::FeaturePython] Constraint010  label="AxialAlignment"  # WARN: FeaturePython — macro-defined, semantics opaque (R4)
  Angle = 0
  AnglePitch = 0
  AngleRoll = 0
  Disabled = false
  Group = -> [ElementLink019,ElementLink020]
  LockAngle = false
  Multiply = false
  TreeRank = 0
  _ConstraintType = 36
  _LinkVersion = 1
  _Parent = -> Constraints
FEATURE [App::FeaturePython] ElementLink019  label="Fix1@As3motorFrame@"  # link proxy (typed FeaturePython)
  LinkTransform = true
  LinkedObject = -> _Element017
  TreeRank = 0
  _LinkVersion = 1
  _Parent = -> Constraint010
FEATURE [Part::FeaturePython] _Element017  label="Fix1@As3motorFrame@"  # link proxy (typed FeaturePython)
  Detach = false
  LinkTransform = true
  LinkedObject = -> Link004 [1.$Fix1.]
  TreeRank = 0
  _LinkVersion = 1
  _Parent = -> Elements
FEATURE [App::FeaturePython] ElementLink020  label="Fix@As3bottom_corner-M3x10@"  # link proxy (typed FeaturePython)
  LinkTransform = true
  LinkedObject = -> _Element018
  TreeRank = 0
  _LinkVersion = 1
  _Parent = -> Constraint010
FEATURE [Part::FeaturePython] _Element018  label="Fix@As3bottom_corner-M3x10@"  # link proxy (typed FeaturePython)
  Detach = false
  LinkTransform = true
  LinkedObject = -> Link [1.$FixM1.]
  TreeRank = 0
  _LinkVersion = 1
  _Parent = -> Elements
FEATURE [App::FeaturePython] Constraint011  label="SameOrientation"  # WARN: FeaturePython — macro-defined, semantics opaque (R4)
  Disabled = false
  Group = -> [ElementLink021,ElementLink022]
  TreeRank = 0
  _ConstraintType = 2
  _LinkVersion = 1
  _Parent = -> Constraints
FEATURE [App::FeaturePython] ElementLink021  label="_Element"  # link proxy (typed FeaturePython)
  LinkTransform = true
  LinkedObject = -> _Element
  TreeRank = 0
  _LinkVersion = 1
  _Parent = -> Constraint011
FEATURE [App::FeaturePython] ElementLink022  label="AppuiH1@As3motorFrame@"  # link proxy (typed FeaturePython)
  LinkTransform = true
  LinkedObject = -> _Element019
  Placement = pos=(-9.8e-15,-1.42e-14,0) rot=(0,0,1;0rad)
  TreeRank = 0
  _LinkVersion = 1
  _Parent = -> Constraint011
FEATURE [Part::FeaturePython] _Element019  label="AppuiH1@As3motorFrame@"  # link proxy (typed FeaturePython)
  Detach = false
  LinkTransform = true
  LinkedObject = -> Link004 [1.$AppuiH1.]
  TreeRank = 0
  _LinkVersion = 1
  _Parent = -> Elements
FEATURE [App::FeaturePython] Constraint012  label="AxialAlignment001"  # WARN: FeaturePython — macro-defined, semantics opaque (R4)
  Angle = 0
  AnglePitch = 0
  AngleRoll = 0
  Disabled = false
  Group = -> [ElementLink023,ElementLink024]
  LockAngle = false
  Multiply = false
  TreeRank = 0
  _ConstraintType = 36
  _LinkVersion = 1
  _Parent = -> Constraints
FEATURE [App::FeaturePython] ElementLink023  label="FixM2@As3bottom_corner-M3x10@"  # link proxy (typed FeaturePython)
  LinkTransform = true
  LinkedObject = -> _Element020
  TreeRank = 0
  _LinkVersion = 1
  _Parent = -> Constraint012
FEATURE [Part::FeaturePython] _Element020  label="FixM2@As3bottom_corner-M3x10@"  # link proxy (typed FeaturePython)
  Detach = false
  LinkTransform = true
  LinkedObject = -> Link [1.$FixM2.]
  TreeRank = 0
  _LinkVersion = 1
  _Parent = -> Elements
FEATURE [App::FeaturePython] ElementLink024  label="Fix2@As3motorFrame@"  # link proxy (typed FeaturePython)
  LinkTransform = true
  LinkedObject = -> _Element021
  TreeRank = 0
  _LinkVersion = 1
  _Parent = -> Constraint012
FEATURE [Part::FeaturePython] _Element021  label="Fix2@As3motorFrame@"  # link proxy (typed FeaturePython)
  Detach = false
  LinkTransform = true
  LinkedObject = -> Link004 [1.$Fix2.]
  TreeRank = 0
  _LinkVersion = 1
  _Parent = -> Elements
FEATURE [App::FeaturePython] Constraint013  label="PlaneCoincident"  # WARN: FeaturePython — macro-defined, semantics opaque (R4)
  Angle = 0
  AnglePitch = 0
  AngleRoll = 0
  Cascade = false
  Disabled = false
  Group = -> [ElementLink025,ElementLink026]
  LockAngle = false
  Multiply = false
  OffsetX = 0
  OffsetY = 0
  TreeRank = 0
  _ConstraintType = 35
  _LinkVersion = 1
  _Parent = -> Constraints
FEATURE [App::FeaturePython] ElementLink025  label="CentreMot@As3NEMA 17@"  # link proxy (typed FeaturePython)
  LinkTransform = true
  LinkedObject = -> _Element022
  TreeRank = 0
  _LinkVersion = 1
  _Parent = -> Constraint013
FEATURE [Part::FeaturePython] _Element022  label="CentreMot@As3NEMA 17@"  # link proxy (typed FeaturePython)
  Detach = false
  LinkTransform = true
  LinkedObject = -> Link005 [1.$CentreMot.]
  TreeRank = 0
  _LinkVersion = 1
  _Parent = -> Elements
FEATURE [App::FeaturePython] ElementLink026  label="CentrMot@As3motorFrame@"  # link proxy (typed FeaturePython)
  LinkTransform = true
  LinkedObject = -> _Element023
  TreeRank = 0
  _LinkVersion = 1
  _Parent = -> Constraint013
FEATURE [Part::FeaturePython] _Element023  label="CentrMot@As3motorFrame@"  # link proxy (typed FeaturePython)
  Detach = false
  LinkTransform = true
  LinkedObject = -> Link004 [1.$CentrMot.]
  TreeRank = 0
  _LinkVersion = 1
  _Parent = -> Elements
FEATURE [App::FeaturePython] Constraint014  label="SameOrientation001"  # WARN: FeaturePython — macro-defined, semantics opaque (R4)
  Disabled = false
  Group = -> [ElementLink027,ElementLink028]
  TreeRank = 0
  _ConstraintType = 2
  _LinkVersion = 1
  _Parent = -> Constraints
FEATURE [App::FeaturePython] ElementLink027  label="FaceH@As3NEMA 17@"  # link proxy (typed FeaturePython)
  LinkTransform = true
  LinkedObject = -> _Element024
  TreeRank = 0
  _LinkVersion = 1
  _Parent = -> Constraint014
FEATURE [Part::FeaturePython] _Element024  label="FaceH@As3NEMA 17@"  # link proxy (typed FeaturePython)
  Detach = false
  LinkTransform = true
  LinkedObject = -> Link005 [1.$FaceH.]
  TreeRank = 0
  _LinkVersion = 1
  _Parent = -> Elements
FEATURE [App::FeaturePython] ElementLink028  label="AppuiH1@As3motorFrame@"  # link proxy (typed FeaturePython)
  LinkTransform = true
  LinkedObject = -> _Element019
  TreeRank = 0
  _LinkVersion = 1
  _Parent = -> Constraint014
FEATURE [App::FeaturePython] Constraint015  label="PlaneAlignment009"  # WARN: FeaturePython — macro-defined, semantics opaque (R4)
  Angle = 0
  AnglePitch = 0
  AngleRoll = 0
  Cascade = false
  Disabled = false
  Group = -> [ElementLink029,ElementLink030]
  LockAngle = false
  TreeRank = 0
  _ConstraintType = 37
  _LinkVersion = 1
  _Parent = -> Constraints
FEATURE [App::FeaturePython] ElementLink029  label="Extrem2@As3V-Slot 20x60x1000 Linear Rail@"  # link proxy (typed FeaturePython)
  LinkTransform = true
  LinkedObject = -> _Element025
  TreeRank = 0
  _LinkVersion = 1
  _Parent = -> Constraint015
FEATURE [Part::FeaturePython] _Element025  label="Extrem2@As3V-Slot 20x60x1000 Linear Rail@"  # link proxy (typed FeaturePython)
  Detach = false
  LinkTransform = true
  LinkedObject = -> Link002 [1.$Extrem2.]
  TreeRank = 0
  _LinkVersion = 1
  _Parent = -> Elements
FEATURE [App::FeaturePython] ElementLink030  label="FaceHsup@As3top_corner@"  # link proxy (typed FeaturePython)
  LinkTransform = true
  LinkedObject = -> _Element026
  TreeRank = 0
  _LinkVersion = 1
  _Parent = -> Constraint015
FEATURE [Part::FeaturePython] _Element026  label="FaceHsup@As3top_corner@"  # link proxy (typed FeaturePython)
  Detach = false
  LinkTransform = true
  LinkedObject = -> Link006 [1.$FaceHsup.]
  TreeRank = 0
  _LinkVersion = 1
  _Parent = -> Elements
FEATURE [App::FeaturePython] Constraint016  label="PlaneAlignment010"  # WARN: FeaturePython — macro-defined, semantics opaque (R4)
  Angle = 0
  AnglePitch = 0
  AngleRoll = 0
  Cascade = false
  Disabled = false
  Group = -> [ElementLink031,ElementLink032]
  LockAngle = false
  TreeRank = 0
  _ConstraintType = 37
  _LinkVersion = 1
  _Parent = -> Constraints
FEATURE [App::FeaturePython] ElementLink031  label="_Element001"  # link proxy (typed FeaturePython)
  LinkTransform = true
  LinkedObject = -> _Element001
  TreeRank = 0
  _LinkVersion = 1
  _Parent = -> Constraint016
FEATURE [App::FeaturePython] ElementLink032  label="AppuiPoteau1@As3top_corner@"  # link proxy (typed FeaturePython)
  LinkTransform = true
  LinkedObject = -> _Element027
  TreeRank = 0
  _LinkVersion = 1
  _Parent = -> Constraint016
FEATURE [Part::FeaturePython] _Element027  label="AppuiPoteau1@As3top_corner@"  # link proxy (typed FeaturePython)
  Detach = false
  LinkTransform = true
  LinkedObject = -> Link006 [1.$AppuiPoteau1.]
  TreeRank = 0
  _LinkVersion = 1
  _Parent = -> Elements
FEATURE [App::FeaturePython] Constraint017  label="PlaneAlignment011"  # WARN: FeaturePython — macro-defined, semantics opaque (R4)
  Angle = 0
  AnglePitch = 0
  AngleRoll = 0
  Cascade = false
  Disabled = false
  Group = -> [ElementLink033,ElementLink034]
  LockAngle = false
  TreeRank = 0
  _ConstraintType = 37
  _LinkVersion = 1
  _Parent = -> Constraints
FEATURE [App::FeaturePython] ElementLink033  label="AppuiPoteau2@As3top_corner@"  # link proxy (typed FeaturePython)
  LinkTransform = true
  LinkedObject = -> _Element028
  TreeRank = 0
  _LinkVersion = 1
  _Parent = -> Constraint017
FEATURE [Part::FeaturePython] _Element028  label="AppuiPoteau2@As3top_corner@"  # link proxy (typed FeaturePython)
  Detach = false
  LinkTransform = true
  LinkedObject = -> Link006 [1.$AppuiPoteau2.]
  TreeRank = 0
  _LinkVersion = 1
  _Parent = -> Elements
FEATURE [App::FeaturePython] ElementLink034  label="_Element003"  # link proxy (typed FeaturePython)
  LinkTransform = true
  LinkedObject = -> _Element003
  TreeRank = 0
  _LinkVersion = 1
  _Parent = -> Constraint017
FEATURE [App::FeaturePython] Constraint018  label="PlaneAlignment014"  # WARN: FeaturePython — macro-defined, semantics opaque (R4)
  Angle = 0
  AnglePitch = 0
  AngleRoll = 0
  Cascade = false
  Disabled = false
  Group = -> [ElementLink035,ElementLink036]
  LockAngle = false
  TreeRank = 0
  _ConstraintType = 37
  _LinkVersion = 1
  _Parent = -> Constraints
FEATURE [App::FeaturePython] ElementLink035  label="Extrem1@As3OpenBeam450mm@#2"  # link proxy (typed FeaturePython)
  LinkTransform = true
  LinkedObject = -> _Element029
  TreeRank = 0
  _LinkVersion = 1
  _Parent = -> Constraint018
FEATURE [Part::FeaturePython] _Element029  label="Extrem1@As3OpenBeam450mm@#2"  # link proxy (typed FeaturePython)
  Detach = false
  LinkTransform = true
  LinkedObject = -> Link003 [Link003_i2.1.$Extrem1.]
  TreeRank = 0
  _LinkVersion = 1
  _Parent = -> Elements
FEATURE [App::FeaturePython] ElementLink036  label="AppuiTravExtr1@As3top_corner@"  # link proxy (typed FeaturePython)
  LinkTransform = true
  LinkedObject = -> _Element030
  TreeRank = 0
  _LinkVersion = 1
  _Parent = -> Constraint018
FEATURE [Part::FeaturePython] _Element030  label="AppuiTravExtr1@As3top_corner@"  # link proxy (typed FeaturePython)
  Detach = false
  LinkTransform = true
  LinkedObject = -> Link006 [1.$AppuiTravExtr1.]
  TreeRank = 0
  _LinkVersion = 1
  _Parent = -> Elements
FEATURE [App::FeaturePython] Constraint019  label="PlaneAlignment012"  # WARN: FeaturePython — macro-defined, semantics opaque (R4)
  Angle = 0
  AnglePitch = 0
  AngleRoll = 0
  Cascade = false
  Disabled = false
  Group = -> [ElementLink037,ElementLink038]
  LockAngle = false
  TreeRank = 0
  _ConstraintType = 37
  _LinkVersion = 1
  _Parent = -> Constraints
FEATURE [App::FeaturePython] ElementLink037  label="FaceLat1@As3OpenBeam450mm@#2"  # link proxy (typed FeaturePython)
  LinkTransform = true
  LinkedObject = -> _Element031
  TreeRank = 0
  _LinkVersion = 1
  _Parent = -> Constraint019
FEATURE [Part::FeaturePython] _Element031  label="FaceLat1@As3OpenBeam450mm@#2"  # link proxy (typed FeaturePython)
  Detach = false
  LinkTransform = true
  LinkedObject = -> Link003 [Link003_i2.1.$FaceLat1.]
  TreeRank = 0
  _LinkVersion = 1
  _Parent = -> Elements
FEATURE [App::FeaturePython] ElementLink038  label="AppuiTrav2v@As3top_corner@"  # link proxy (typed FeaturePython)
  LinkTransform = true
  LinkedObject = -> _Element032
  TreeRank = 0
  _LinkVersion = 1
  _Parent = -> Constraint019
FEATURE [Part::FeaturePython] _Element032  label="AppuiTrav2v@As3top_corner@"  # link proxy (typed FeaturePython)
  Detach = false
  LinkTransform = true
  LinkedObject = -> Link006 [1.$AppuiTrav2v.]
  TreeRank = 0
  _LinkVersion = 1
  _Parent = -> Elements
FEATURE [App::FeaturePython] Constraint020  label="PlaneAlignment013"  # WARN: FeaturePython — macro-defined, semantics opaque (R4)
  Angle = 0
  AnglePitch = 0
  AngleRoll = 0
  Cascade = false
  Disabled = false
  Group = -> [ElementLink039,ElementLink040]
  LockAngle = false
  TreeRank = 0
  _ConstraintType = 37
  _LinkVersion = 1
  _Parent = -> Constraints
FEATURE [App::FeaturePython] ElementLink039  label="AppuiTrav1h@As3top_corner@"  # link proxy (typed FeaturePython)
  LinkTransform = true
  LinkedObject = -> _Element033
  TreeRank = 0
  _LinkVersion = 1
  _Parent = -> Constraint020
FEATURE [Part::FeaturePython] _Element033  label="AppuiTrav1h@As3top_corner@"  # link proxy (typed FeaturePython)
  Detach = false
  LinkTransform = true
  LinkedObject = -> Link006 [1.$AppuiTrav1h.]
  TreeRank = 0
  _LinkVersion = 1
  _Parent = -> Elements
FEATURE [App::FeaturePython] ElementLink040  label="FaceHoriz1@As3OpenBeam450mm@#2"  # link proxy (typed FeaturePython)
  LinkTransform = true
  LinkedObject = -> _Element034
  TreeRank = 0
  _LinkVersion = 1
  _Parent = -> Constraint020
FEATURE [Part::FeaturePython] _Element034  label="FaceHoriz1@As3OpenBeam450mm@#2"  # link proxy (typed FeaturePython)
  Detach = false
  LinkTransform = true
  LinkedObject = -> Link003 [Link003_i2.1.$FaceHoriz1.]
  TreeRank = 0
  _LinkVersion = 1
  _Parent = -> Elements
FEATURE [App::FeaturePython] Constraint021  label="PlaneAlignment015"  # WARN: FeaturePython — macro-defined, semantics opaque (R4)
  Angle = 0
  AnglePitch = 0
  AngleRoll = 0
  Cascade = false
  Disabled = false
  Group = -> [ElementLink041,ElementLink042]
  LockAngle = false
  TreeRank = 0
  _ConstraintType = 37
  _LinkVersion = 1
  _Parent = -> Constraints
FEATURE [App::FeaturePython] ElementLink041  label="_Element"  # link proxy (typed FeaturePython)
  LinkTransform = true
  LinkedObject = -> _Element
  TreeRank = 0
  _LinkVersion = 1
  _Parent = -> Constraint021
FEATURE [App::FeaturePython] ElementLink042  label="Etrem1@As3V-Slot 20x40x1000 Linear Rail@"  # link proxy (typed FeaturePython)
  LinkTransform = true
  LinkedObject = -> _Element035
  TreeRank = 0
  _LinkVersion = 1
  _Parent = -> Constraint021
FEATURE [Part::FeaturePython] _Element035  label="Etrem1@As3V-Slot 20x40x1000 Linear Rail@"  # link proxy (typed FeaturePython)
  Detach = false
  LinkTransform = true
  LinkedObject = -> Link001 [1.$Etrem1.]
  TreeRank = 0
  _LinkVersion = 1
  _Parent = -> Elements
FEATURE [App::FeaturePython] Constraint022  label="PlaneAlignment016"  # WARN: FeaturePython — macro-defined, semantics opaque (R4)
  Angle = 0
  AnglePitch = 0
  AngleRoll = 0
  Cascade = false
  Disabled = false
  Group = -> [ElementLink043,ElementLink044]
  LockAngle = false
  TreeRank = 0
  _ConstraintType = 37
  _LinkVersion = 1
  _Parent = -> Constraints
FEATURE [App::FeaturePython] ElementLink043  label="FaceVref2@As3V-Slot 20x60x1000 Linear Rail@"  # link proxy (typed FeaturePython)
  LinkTransform = true
  LinkedObject = -> _Element036
  TreeRank = 0
  _LinkVersion = 1
  _Parent = -> Constraint022
FEATURE [Part::FeaturePython] _Element036  label="FaceVref2@As3V-Slot 20x60x1000 Linear Rail@"  # link proxy (typed FeaturePython)
  Detach = false
  LinkTransform = true
  LinkedObject = -> Link002 [1.$FaceVref2.]
  TreeRank = 0
  _LinkVersion = 1
  _Parent = -> Elements
FEATURE [App::FeaturePython] ElementLink044  label="Lat1@As3V-Slot 20x40x1000 Linear Rail@"  # link proxy (typed FeaturePython)
  LinkTransform = true
  LinkedObject = -> _Element037
  TreeRank = 0
  _LinkVersion = 1
  _Parent = -> Constraint022
FEATURE [Part::FeaturePython] _Element037  label="Lat1@As3V-Slot 20x40x1000 Linear Rail@"  # link proxy (typed FeaturePython)
  Detach = false
  LinkTransform = true
  LinkedObject = -> Link001 [1.$Lat1.]
  TreeRank = 0
  _LinkVersion = 1
  _Parent = -> Elements
FEATURE [App::FeaturePython] Constraint023  label="PlaneAlignment017"  # WARN: FeaturePython — macro-defined, semantics opaque (R4)
  Angle = 0
  AnglePitch = 0
  AngleRoll = 0
  Cascade = false
  Disabled = false
  Group = -> [ElementLink045,ElementLink046]
  LockAngle = false
  TreeRank = 0
  _ConstraintType = 37
  _LinkVersion = 1
  _Parent = -> Constraints
FEATURE [App::FeaturePython] ElementLink045  label="FaceRef@As3V-Slot 20x40x1000 Linear Rail@"  # link proxy (typed FeaturePython)
  LinkTransform = true
  LinkedObject = -> _Element038
  TreeRank = 0
  _LinkVersion = 1
  _Parent = -> Constraint023
FEATURE [Part::FeaturePython] _Element038  label="FaceRef@As3V-Slot 20x40x1000 Linear Rail@"  # link proxy (typed FeaturePython)
  Detach = false
  LinkTransform = true
  LinkedObject = -> Link001 [1.$FaceRef.]
  TreeRank = 0
  _LinkVersion = 1
  _Parent = -> Elements
FEATURE [App::FeaturePython] ElementLink046  label="AppuiLatPoteau22@As3top_corner@"  # link proxy (typed FeaturePython)
  LinkTransform = true
  LinkedObject = -> _Element039
  TreeRank = 0
  _LinkVersion = 1
  _Parent = -> Constraint023
FEATURE [Part::FeaturePython] _Element039  label="AppuiLatPoteau22@As3top_corner@"  # link proxy (typed FeaturePython)
  Detach = false
  LinkTransform = true
  LinkedObject = -> Link006 [1.$AppuiLatPoteau22.]
  TreeRank = 0
  _LinkVersion = 1
  _Parent = -> Elements
FEATURE [App::FeaturePython] Constraint024  label="PlaneAlignment018"  # WARN: FeaturePython — macro-defined, semantics opaque (R4)
  Angle = 0
  AnglePitch = 0
  AngleRoll = 0
  Cascade = false
  Disabled = false
  Group = -> [ElementLink047,ElementLink048]
  LockAngle = false
  TreeRank = 0
  _ConstraintType = 37
  _LinkVersion = 1
  _Parent = -> Constraints
FEATURE [App::FeaturePython] ElementLink047  label="_Element"  # link proxy (typed FeaturePython)
  LinkTransform = true
  LinkedObject = -> _Element
  TreeRank = 0
  _LinkVersion = 1
  _Parent = -> Constraint024
FEATURE [App::FeaturePython] ElementLink048  label="Extrem1@As3MGNR9R900CM-HiwinCorporation-3D-10-31-2021@"  # link proxy (typed FeaturePython)
  LinkTransform = true
  LinkedObject = -> _Element040
  TreeRank = 0
  _LinkVersion = 1
  _Parent = -> Constraint024
FEATURE [Part::FeaturePython] _Element040  label="Extrem1@As3MGNR9R900CM-HiwinCorporation-3D-10-31-2021@"  # link proxy (typed FeaturePython)
  Detach = false
  LinkTransform = true
  LinkedObject = -> Link007 [1.$Extrem1.]
  TreeRank = 0
  _LinkVersion = 1
  _Parent = -> Elements
FEATURE [App::FeaturePython] Constraint025  label="PlaneAlignment019"  # WARN: FeaturePython — macro-defined, semantics opaque (R4)
  Angle = 0
  AnglePitch = 0
  AngleRoll = 0
  Cascade = false
  Disabled = false
  Group = -> [ElementLink049,ElementLink050]
  LockAngle = false
  Offset = 39.5
  TreeRank = 0
  _ConstraintType = 37
  _LinkVersion = 1
  _Parent = -> Constraints
FEATURE [App::FeaturePython] ElementLink049  label="Ref@As3MGNR9R900CM-HiwinCorporation-3D-10-31-2021@"  # link proxy (typed FeaturePython)
  LinkTransform = true
  LinkedObject = -> _Element041
  TreeRank = 0
  _LinkVersion = 1
  _Parent = -> Constraint025
FEATURE [Part::FeaturePython] _Element041  label="Ref@As3MGNR9R900CM-HiwinCorporation-3D-10-31-2021@"  # link proxy (typed FeaturePython)
  Detach = false
  LinkTransform = true
  LinkedObject = -> Link007 [1.$Ref.]
  TreeRank = 0
  _LinkVersion = 1
  _Parent = -> Elements
FEATURE [App::FeaturePython] ElementLink050  label="Lat1@As3V-Slot 20x40x1000 Linear Rail@"  # link proxy (typed FeaturePython)
  LinkTransform = true
  LinkedObject = -> _Element037
  TreeRank = 0
  _LinkVersion = 1
  _Parent = -> Constraint025
FEATURE [App::FeaturePython] Constraint026  label="PlaneAlignment020"  # WARN: FeaturePython — macro-defined, semantics opaque (R4)
  Angle = 0
  AnglePitch = 0
  AngleRoll = 0
  Cascade = false
  Disabled = false
  Group = -> [ElementLink051,ElementLink052]
  LockAngle = false
  Offset = 5.5
  TreeRank = 0
  _ConstraintType = 37
  _LinkVersion = 1
  _Parent = -> Constraints
FEATURE [App::FeaturePython] ElementLink051  label="Lat@As3MGNR9R900CM-HiwinCorporation-3D-10-31-2021@"  # link proxy (typed FeaturePython)
  LinkTransform = true
  LinkedObject = -> _Element042
  TreeRank = 0
  _LinkVersion = 1
  _Parent = -> Constraint026
FEATURE [Part::FeaturePython] _Element042  label="Lat@As3MGNR9R900CM-HiwinCorporation-3D-10-31-2021@"  # link proxy (typed FeaturePython)
  Detach = false
  LinkTransform = true
  LinkedObject = -> Link007 [1.$Lat.]
  TreeRank = 0
  _LinkVersion = 1
  _Parent = -> Elements
FEATURE [App::FeaturePython] ElementLink052  label="FaceRef@As3V-Slot 20x40x1000 Linear Rail@"  # link proxy (typed FeaturePython)
  LinkTransform = true
  LinkedObject = -> _Element038
  TreeRank = 0
  _LinkVersion = 1
  _Parent = -> Constraint026
FEATURE [Part::FeaturePython] Element  label="Fix3@As3motorFrame@"  # link proxy (typed FeaturePython)
  Detach = false
  LinkTransform = true
  LinkedObject = -> Link004 [1.$Fix3.]
  TreeRank = 0
  _LinkVersion = 1
  _Parent = -> Elements
FEATURE [Part::FeaturePython] Element001  label="Fix4@As3motorFrame@"  # link proxy (typed FeaturePython)
  Detach = false
  LinkTransform = true
  LinkedObject = -> Link004 [1.$Fix4.]
  TreeRank = 0
  _LinkVersion = 1
  _Parent = -> Elements
FEATURE [Part::FeaturePython] Element002  label="Fix@As3MGNR9R900CM-HiwinCorporation-3D-10-31-2021@"  # link proxy (typed FeaturePython)
  Detach = false
  LinkTransform = true
  LinkedObject = -> Link007 [1.$Fix.]
  TreeRank = 0
  _LinkVersion = 1
  _Parent = -> Elements
